# Revit family: URA_Eclairage_de_Securite_URALIFE
name_source: partatom
category: Luminaires
units: mm (PartAtom-declared; Revit-internal decimal feet)

## family parameters
Cote de connecteur circulaire = Utiliser le diamètre
Couper avec des vides une fois chargée = Non
Hôte = Face
Partagée = Non
Point de calcul de pièce = Non
Source d'éclairage = Oui
Type d'élément = Normal

## types (15) — shared parameters
Angle de l'inclinaison = 60.00°
CLASSE_DE_PROTECTION = II
CLASSE_DE_PROTECTION_(IP) = IP43
COULEUR_DU_BOITIER = blanc
Condition Générale d'Utilisation = https://export.legrand.com
DISTANCE_DE_RECONNAISSANCE = 15
Elévation par défaut = 1219 mm
FORMAT_PRODUIT = rectangle
Fichier de distribution photométrique = generic
Filtre de couleur = 16777215
Gradation des changements de température de couleur de lampe = <Aucun>
INSTALLATION_DE_SURVEILLANCE = auto-test automatique
MATERIAU_DU_BOITIER = plastique
MATERIAU_DU_COUVERCLE = plastique transparent
SOURCE_LUMINEUSE = LED non interchangeable
TYPE_DE_MONTAGE = pose murale en saillie

## per-type parameters (varying)
| type | ADAPTE_AU_TYPE_DE_MARQUAGE | ALIMENTATION | CATEGORIE_PRODUIT | DUREE_DE_GARANTIE_BAES_COMPLET | ETAT_DES_ACCUS | FLUX_LUMINEUX_EN_MODE_D'URGENCE | FONCTION | HAUTEUR/PROFONDEUR | LARGEUR | LONGUEUR | Longueur | PUISSANCE_DE_LA_LAMPE | REFERENCE_ARTICLE | REF_BATTERIE_DE_RECHANGE | RESERVE_DE_MARCHE | TENSION_NOMINALE_(MAX) | TENSION_NOMINALE_(MIN) | TYPE_DE_COMMUTATION | TYPE_DE_TENSION |
| BAEH URALIFE S.SATI | feuillet/plaque inséré(e) | décentralisé (batterie individuelle) | Autonome | 4 | NiCd | 8 | BAEH | 55.5 | 117.9 | 239.14 | 239 mm  [stored 0.784121 ft] | 0.04 | 118138 | 111901 | 5 | 253 | 207 | mode veille | CA |
| BAEH URALIFE ADR | feuillet/plaque inséré(e) | décentralisé (batterie individuelle) | Autonome | 4 | NiCd | 8 | BAEH | 55.5 | 117.9 | 239.14 | 239 mm  [stored 0.784121 ft] | 0.04 | 118139 | 111901 | 5 | 253 | 207 | mode veille | CA |
| BAES URALIFE EVAC S.SATI | feuillet/plaque inséré(e) | décentralisé (batterie individuelle) | Autonome | 4 | NiCd | 45 | Evac | 55.5 | 117.9 | 239.14 | 239 mm  [stored 0.784121 ft] | 0.6 | 118218 | 111901 | 1 | 253 | 207 | mode veille | CA |
| BAES URALIFE EVAC ADR | feuillet/plaque inséré(e) | décentralisé (batterie individuelle) | Autonome | 4 | NiCd | 45 | Evac | 55.5 | 117.9 | 239.14 | 239 mm  [stored 0.784121 ft] | 0.6 | 118219 | 111901 | 1 | 253 | 207 | mode veille | CA |
| BAES URALIFE AMB S.SATI |  | décentralisé (batterie individuelle) | Autonome | 4 | NiCd | 400 | Amb | 58.5 | 118.25 | 289.05 | 289 mm  [stored 0.948163 ft] | 4 | 118228 | 2*111902 | 1 | 253 | 207 | mode veille | CA |
| BAES URALIFE AMB ADR |  | décentralisé (batterie individuelle) | Autonome | 4 | NiCd | 400 | Amb | 58.5 | 118.25 | 289.05 | 289 mm  [stored 0.948163 ft] | 6.6 | 118229 | 2*111902 | 1 | 253 | 207 | mode veille | CA |
| BAES AMB PERMANENT SATI ADR |  | décentralisé (batterie individuelle) | Autonome | 2 | NiCd | 450 | Amb | 57 | 164.5 | 261.2 | 239 mm  [stored 0.784121 ft] | 6 | 118239 | 2*111902 | 1 | 253 | 207 | mode veille | CA |
| BAES + BAEH URALIFE S.SATI | feuillet/plaque inséré(e) | décentralisé (batterie individuelle) | Autonome | 4 | NiCd | 45 | BAES+BAEH | 55.5 | 117.9 | 239.14 | 239 mm  [stored 0.784121 ft] | 0.8 | 118248 | 2*111901 | 1 | 253 | 207 | mode veille | CA |
| BAES + BAEH URALIFE ADR | feuillet/plaque inséré(e) | décentralisé (batterie individuelle) | Autonome | 4 | NiCd | 45 | BAES+BAEH | 55.5 | 117.9 | 239.14 | 239 mm  [stored 0.784121 ft] | 0.8 | 118249 | 2*111901 | 1 | 253 | 207 | mode veille | CA |
| BAES + DBR URALIFE SATI | feuillet/plaque inséré(e) | décentralisé (batterie individuelle) | Autonome | 4 | NiCd | 45 | DBR | 55.5 | 117.9 | 239.14 | 239 mm  [stored 0.784121 ft] | 1 | 118257 | 111901 | 1 | 253 | 207 | mode veille | CA |
| BAES + DBR URALIFE ADR | feuillet/plaque inséré(e) | décentralisé (batterie individuelle) | Autonome | 4 | NiCd | 45 | DBR | 55.5 | 117.9 | 239.14 | 239 mm  [stored 0.784121 ft] | 1 | 118259 | 111901 | 1 | 253 | 207 | mode veille | CA |
| LSC URALIFE EVAC 110/220/230 | feuillet/plaque inséré(e) | central (batterie centrale) | LSC | 4 | non applicable | 45 | Evac | 55.5 | 117.9 | 239.14 | 239 mm  [stored 0.784121 ft] | 0.8 | 128214 |  |  | 230 | 110 | circuit permanent/circuit de secours | CA/CC |
| LSC URALIFE AMB 110/220/230 |  | central (batterie centrale) | LSC | 4 | non applicable | 400 | Amb | 58.5 | 118.25 | 289.05 | 289 mm  [stored 0.948163 ft] | 6.6 | 128224 |  |  | 230 | 110 | circuit permanent/circuit de secours | CA/CC |
| LSC URALIFE EVAC 24/48 | feuillet/plaque inséré(e) | central (batterie centrale) | LSC | 4 | non applicable | 45 | Evac | 55.5 | 117.9 | 239.14 | 239 mm  [stored 0.784121 ft] | 0.8 | 128215 |  |  | 48 | 24 | circuit permanent/circuit de secours | CC |
| LSC URALIFE AMB 24/48 |  | central (batterie centrale) | LSC | 4 | non applicable | 400 | Amb | 58.5 | 118.25 | 289.05 | 289 mm  [stored 0.948163 ft] | 6.6 | 128225 |  |  | 48 | 24 | circuit permanent/circuit de secours | CC |

note: column(s) folded — value = type name in every type: DESIGNATION_ARTICLE

note: [stored X ft] marks values corroborated as IEEE doubles in the binary element streams (Revit-internal decimal feet)
